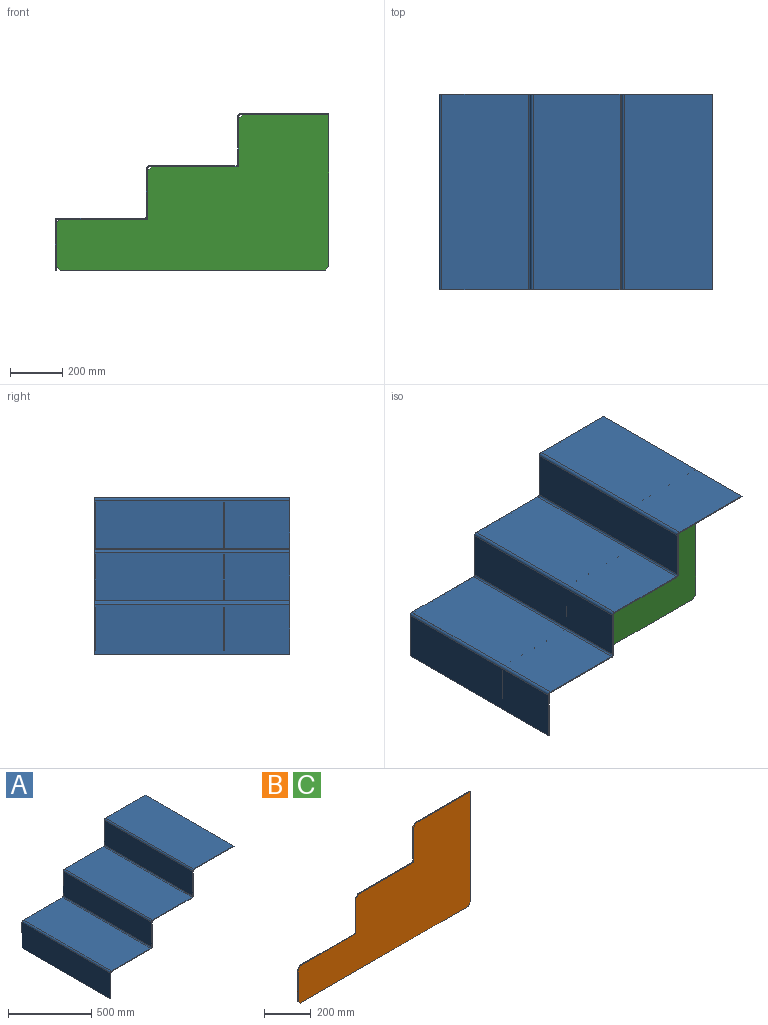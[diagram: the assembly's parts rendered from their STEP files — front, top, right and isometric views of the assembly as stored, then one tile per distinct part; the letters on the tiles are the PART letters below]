
ASSEMBLY  parts=3 mates=1
PART A: 46 faces, bbox 1050x750x600 mm
  f0: plane 189.7x4mm, normal (0,1,0), area 758.8mm2, adj f2,f3,f4,f43
  f1: plane 189.7x4mm, normal (0,-1,0), area 758.8mm2, adj f2,f3,f4,f42
  f2: plane 750x4mm, normal (0,0,-1), area 3000mm2, adj f0,f1,f3,f4
  f3: plane 750x189.7mm, normal (1,0,0), area 142275mm2, adj f0,f1,f2,f45
  f4: plane 750x189.7mm, normal (-1,0,0), area 142275mm2, adj f0,f1,f2,f44
  f5: plane 333.4x4mm, normal (0,1,0), area 1333.6mm2, adj f7,f8,f39,f43
  f6: plane 333.4x4mm, normal (0,-1,0), area 1333.6mm2, adj f7,f8,f38,f42
  f7: plane 750x333.4mm, normal (0,0,-1), area 250050mm2, adj f5,f6,f40,f45
  f8: plane 750x333.4mm, normal (0,0,1), area 250050mm2, adj f5,f6,f41,f44
  f9: plane 183.4x4mm, normal (0,1,0), area 733.6mm2, adj f11,f12,f35,f39
  f10: plane 183.4x4mm, normal (0,-1,0), area 733.6mm2, adj f11,f12,f34,f38
  f11: plane 750x183.4mm, normal (1,0,0), area 137550mm2, adj f9,f10,f37,f40
  f12: plane 750x183.4mm, normal (-1,0,0), area 137550mm2, adj f9,f10,f36,f41
  f13: plane 333.4x4mm, normal (0,1,0), area 1333.6mm2, adj f15,f16,f31,f35
  f14: plane 333.4x4mm, normal (0,-1,0), area 1333.6mm2, adj f15,f16,f30,f34
  f15: plane 750x333.4mm, normal (0,0,-1), area 250050mm2, adj f13,f14,f32,f37
  f16: plane 750x333.4mm, normal (0,0,1), area 250050mm2, adj f13,f14,f33,f36
  f17: plane 183.4x4mm, normal (0,1,0), area 733.6mm2, adj f19,f20,f27,f31
  f18: plane 183.4x4mm, normal (0,-1,0), area 733.6mm2, adj f19,f20,f26,f30
  f19: plane 750x183.4mm, normal (1,0,0), area 137550mm2, adj f17,f18,f29,f32
  f20: plane 750x183.4mm, normal (-1,0,0), area 137550mm2, adj f17,f18,f28,f33
  f21: plane 339.7x4mm, normal (0,1,0), area 1358.8mm2, adj f22,f24,f25,f27
  f22: plane 750x4mm, normal (1,0,0), area 3000mm2, adj f21,f23,f24,f25
  f23: plane 339.7x4mm, normal (0,-1,0), area 1358.8mm2, adj f22,f24,f25,f26
  f24: plane 750x339.7mm, normal (0,0,-1), area 254775mm2, adj f21,f22,f23,f29
  f25: plane 750x339.7mm, normal (0,0,1), area 254775mm2, adj f21,f22,f23,f28
  f26: plane 10.3x10.3mm, normal (0,-1,0), area 52.2mm2, adj f18,f23,f28,f29
  f27: plane 10.3x10.3mm, normal (0,1,0), area 52.2mm2, adj f17,f21,f28,f29
  f28: cylinder r=10.3mm len=750mm, axis (0,-1,0), area 12134.4mm2, adj f20,f25,f26,f27
  f29: cylinder r=6.3mm len=750mm, axis (0,-1,0), area 7422mm2, adj f19,f24,f26,f27
  f30: plane 10.3x10.3mm, normal (0,-1,0), area 52.2mm2, adj f14,f18,f32,f33
  f31: plane 10.3x10.3mm, normal (0,1,0), area 52.2mm2, adj f13,f17,f32,f33
  f32: cylinder r=10.3mm len=750mm, axis (0,-1,0), area 12134.4mm2, adj f15,f19,f30,f31
  f33: cylinder r=6.3mm len=750mm, axis (0,-1,0), area 7422mm2, adj f16,f20,f30,f31
  f34: plane 10.3x10.3mm, normal (0,-1,0), area 52.2mm2, adj f10,f14,f36,f37
  f35: plane 10.3x10.3mm, normal (0,1,0), area 52.2mm2, adj f9,f13,f36,f37
  f36: cylinder r=10.3mm len=750mm, axis (0,-1,0), area 12134.4mm2, adj f12,f16,f34,f35
  f37: cylinder r=6.3mm len=750mm, axis (0,-1,0), area 7422mm2, adj f11,f15,f34,f35
  f38: plane 10.3x10.3mm, normal (0,-1,0), area 52.2mm2, adj f6,f10,f40,f41
  f39: plane 10.3x10.3mm, normal (0,1,0), area 52.2mm2, adj f5,f9,f40,f41
  f40: cylinder r=10.3mm len=750mm, axis (0,-1,0), area 12134.4mm2, adj f7,f11,f38,f39
  f41: cylinder r=6.3mm len=750mm, axis (0,-1,0), area 7422mm2, adj f8,f12,f38,f39
  f42: plane 10.3x10.3mm, normal (0,-1,0), area 52.2mm2, adj f1,f6,f44,f45
  f43: plane 10.3x10.3mm, normal (0,1,0), area 52.2mm2, adj f0,f5,f44,f45
  f44: cylinder r=10.3mm len=750mm, axis (0,-1,0), area 12134.4mm2, adj f4,f8,f42,f43
  f45: cylinder r=6.3mm len=750mm, axis (0,-1,0), area 7422mm2, adj f3,f7,f42,f43
PART B: 15 faces, bbox 1046x4x596 mm
  f0: plane 166x4mm, normal (-1,0,0), area 664mm2, adj f8,f9,f12,f14
  f1: plane 1016x4mm, normal (0,0,-1), area 4064mm2, adj f8,f9,f11,f12
  f2: plane 581x4mm, normal (1,0,0), area 2324mm2, adj f3,f8,f9,f11
  f3: plane 331x4mm, normal (0,0,1), area 1324mm2, adj f2,f8,f9,f10
  f4: plane 185x4mm, normal (-1,0,0), area 740mm2, adj f5,f8,f9,f10
  f5: plane 335x4mm, normal (0,0,1), area 1340mm2, adj f4,f8,f9,f13
  f6: plane 185x4mm, normal (-1,0,0), area 740mm2, adj f7,f8,f9,f13
  f7: plane 335x4mm, normal (0,0,1), area 1340mm2, adj f6,f8,f9,f14
  f8: plane 1046x596mm, normal (0,-1,0), area 412853.5mm2, adj f0,f1,f2,f3,f4,f5,f6,f7
  f9: plane 1046x596mm, normal (0,1,0), area 412853.5mm2, adj f0,f1,f2,f3,f4,f5,f6,f7
  f10: plane 15x15mm, normal (-0.71,0,0.71), area 84.9mm2, adj f3,f4,f8,f9
  f11: plane 15x15mm, normal (0.71,0,-0.71), area 84.9mm2, adj f1,f2,f8,f9
  f12: plane 15x15mm, normal (-0.71,0,-0.71), area 84.9mm2, adj f0,f1,f8,f9
  f13: plane 15x15mm, normal (-0.71,0,0.71), area 84.9mm2, adj f5,f6,f8,f9
  f14: plane 15x15mm, normal (-0.71,0,0.71), area 84.9mm2, adj f0,f7,f8,f9
PART C: same geometry as B
PLACE A t=(-313.9,364.38,-59.69)mm
PLACE B t=(-309.9,364.38,-59.69)mm
PLACE C t=(-309.9,-131.62,-59.69)mm
MATE parallel C.f8 <-> A.f14  axis (0,-1,0) through (330.91,-135.62,171.59)mm
